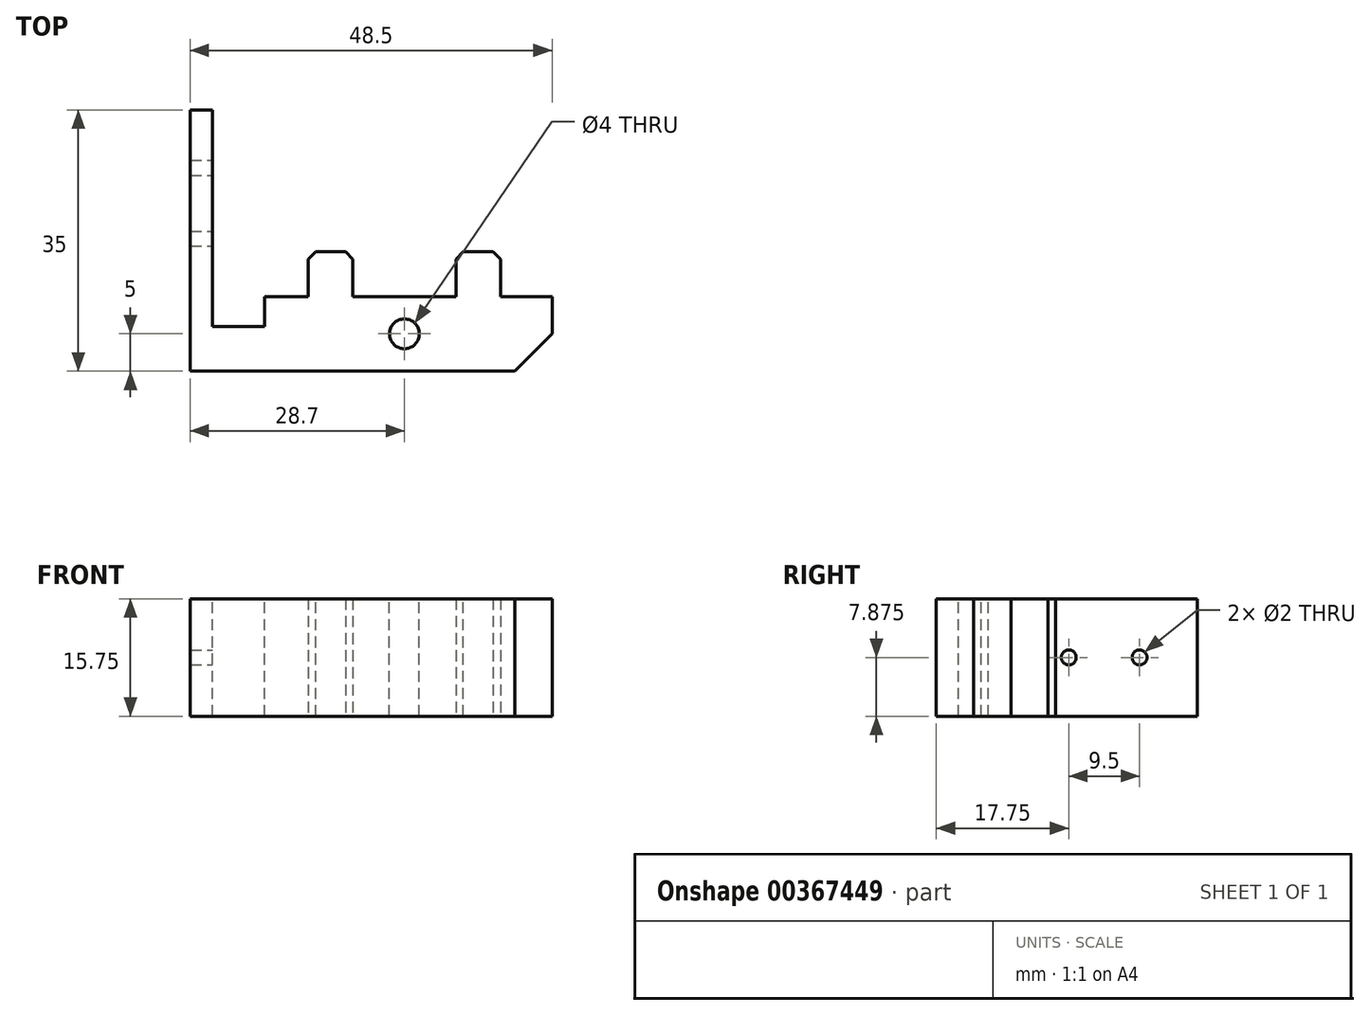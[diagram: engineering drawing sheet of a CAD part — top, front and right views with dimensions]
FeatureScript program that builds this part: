
annotation { "Feature Type Name" : "Feature", "Feature Type Description" : "" }
export const myFeature = defineFeature(function(context is Context, id is Id, definition is map)
    precondition{}
    {
        {
            var Q0;
            Q0=qCreatedBy(makeId("Top.planeOp"),FACE);
            var sketch = newSketch(context, id + "F0", { "sketchPlane" : qUnion([Q0])});
            skLineSegment(sketch, "E0", {"start": v(44.5, 0) * mm, "end": v(44.5, 10) * mm});
            skLineSegment(sketch, "E1", {"start": v(44.5, 10) * mm, "end": v(37.6, 10) * mm});
            skLineSegment(sketch, "E2", {"start": v(37.6, 10) * mm, "end": v(37.6, 16) * mm});
            skLineSegment(sketch, "E3", {"start": v(37.6, 16) * mm, "end": v(31.6, 16) * mm});
            skLineSegment(sketch, "E4", {"start": v(31.6, 16) * mm, "end": v(31.6, 10) * mm});
            skLineSegment(sketch, "E5", {"start": v(31.6, 10) * mm, "end": v(17.8, 10) * mm});
            skLineSegment(sketch, "E6", {"start": v(17.8, 10) * mm, "end": v(17.8, 16) * mm});
            skLineSegment(sketch, "E7", {"start": v(17.8, 16) * mm, "end": v(11.8, 16) * mm});
            skLineSegment(sketch, "E8", {"start": v(11.8, 16) * mm, "end": v(11.8, 10) * mm});
            skLineSegment(sketch, "E9", {"start": v(11.8, 10) * mm, "end": v(0, 10) * mm});
            skLineSegment(sketch, "E10", {"start": v(0, 0) * mm, "end": v(44.5, 0) * mm});
            skLineSegment(sketch, "E11", {"start": v(0, 10) * mm, "end": v(0, 0) * mm});
            skSolve(sketch);
        }
        {
            var Q0;
            Q0=qSketchRegion(id+"F0",true);
            extrude(context, id + "F1", {"entities" : qUnion([Q0]), "depth" : 15.75 * mm});
        }
        {
            var Q0;
            Q0=makeQuery(id+"F1.opExtrude","SWEPT_FACE",FACE,{"disambiguationData":[OSD([sQuery(id+"F0.wireOp",EDGE,"E10")])]});
            var sketch = newSketch(context, id + "F2", { "sketchPlane" : qUnion([Q0])});
            skLineSegment(sketch, "E12", {"start": v(0, 12.75) * mm, "end": v(15, 12.75) * mm});
            skLineSegment(sketch, "E13", {"start": v(15, 12.75) * mm, "end": v(15, 3) * mm});
            skLineSegment(sketch, "E14", {"start": v(15, 3) * mm, "end": v(0, 3) * mm});
            skLineSegment(sketch, "E15", {"start": v(0, 12.75) * mm, "end": v(0, 3) * mm});
            skSolve(sketch);
        }
        {
            var Q0;
            Q0=makeQuery(id+"F1.opExtrude","CAP_FACE",FACE,{"disambiguationData":[OSD([sQuery(id+"F0.wireOp",EDGE,"E0"),sQuery(id+"F0.wireOp",EDGE,"E1"),sQuery(id+"F0.wireOp",EDGE,"E2"),sQuery(id+"F0.wireOp",EDGE,"E3"),sQuery(id+"F0.wireOp",EDGE,"E4"),sQuery(id+"F0.wireOp",EDGE,"E5"),sQuery(id+"F0.wireOp",EDGE,"E6"),sQuery(id+"F0.wireOp",EDGE,"E7"),sQuery(id+"F0.wireOp",EDGE,"E8"),sQuery(id+"F0.wireOp",EDGE,"E9"),sQuery(id+"F0.wireOp",EDGE,"E10"),sQuery(id+"F0.wireOp",EDGE,"E11")])],"isStart":false});
            var sketch = newSketch(context, id + "F3", { "sketchPlane" : qUnion([Q0])});
            skPoint(sketch, "E16", {"position": v(24.7, 5) * mm});
            skPoint(sketch, "E16.positionSnap0", {"position": v(44.5, 5) * mm});
            skPoint(sketch, "E16.positionSnap1", {"position": v(24.7, 10) * mm});
            skSolve(sketch);
        }
        {
            var Q0;
            Q0=sQuery(id+"F3.wireOp",VERTEX,"E16");
            var Q1;
            Q1=makeQuery(id+"F1.opExtrude","SWEPT_BODY",BODY,{"disambiguationData":[OSD([sQuery(id+"F0.wireOp",EDGE,"E0"),sQuery(id+"F0.wireOp",EDGE,"E1"),sQuery(id+"F0.wireOp",EDGE,"E2"),sQuery(id+"F0.wireOp",EDGE,"E3"),sQuery(id+"F0.wireOp",EDGE,"E4"),sQuery(id+"F0.wireOp",EDGE,"E5"),sQuery(id+"F0.wireOp",EDGE,"E6"),sQuery(id+"F0.wireOp",EDGE,"E7"),sQuery(id+"F0.wireOp",EDGE,"E8"),sQuery(id+"F0.wireOp",EDGE,"E9"),sQuery(id+"F0.wireOp",EDGE,"E10"),sQuery(id+"F0.wireOp",EDGE,"E11")])]});
            hole(context, id + "F4", {"style" : HoleStyle.SIMPLE, "endStyle" : HoleEndStyle.THROUGH, "holeDiameter" : 4 * mm, "locations" : qUnion([Q0]), "scope" : qUnion([Q1]), "isTappedThrough" : true});
        }
        {
            var Q0;
            Q0=makeQuery(id+"F1.opExtrude","SWEPT_FACE",FACE,{"disambiguationData":[OSD([sQuery(id+"F0.wireOp",EDGE,"E11")])]});
            extrude(context, id + "F5", {"entities" : qUnion([Q0]), "operationType" : NewBodyOperationType.ADD, "depth" : 3 * mm});
        }
        {
            var Q0;
            {var subQ0=sQuery(id+"F0.wireOp",EDGE,"E9");Q0=makeQuery(id+"F5.boolean.opBoolean","MERGE",FACE,{"derivedFrom":[makeQuery(id+"F1.opExtrude","SWEPT_FACE",FACE,{"disambiguationData":[OSD([subQ0])]}),makeQuery(id+"F5.opExtrude","SWEPT_FACE",FACE,{"disambiguationData":[OSD([subQ0,sQuery(id+"F0.wireOp",EDGE,"E11")])]})]});}
            var sketch = newSketch(context, id + "F6", { "sketchPlane" : qUnion([Q0])});
            skLineSegment(sketch, "E17", {"start": v(0, 0) * mm, "end": v(0, 15.75) * mm});
            skSolve(sketch);
        }
        {
            var Q0;
            {var subQ0=sQuery(id+"F6.wireOp",EDGE,"E17");Q0=makeQuery(id+"F6.imprint","IMPRINT",FACE,{"disambiguationData":[TD([[makeQuery(id+"F6.imprint","IMPRINT",EDGE,{"derivedFrom":subQ0}),-1.0]])]});}
            extrude(context, id + "F7", {"entities" : qUnion([Q0]), "operationType" : NewBodyOperationType.ADD, "depth" : 25 * mm});
        }
        {
            var Q0;
            Q0=makeQuery(id+"F7.opExtrude","SWEPT_FACE",FACE,{"disambiguationData":[OSD([sQuery(id+"F6.wireOp",EDGE,"E17")])]});
            var sketch = newSketch(context, id + "F8", { "sketchPlane" : qUnion([Q0])});
            skPoint(sketch, "E18", {"position": v(27.25, 7.88) * mm});
            skPoint(sketch, "E18.positionSnap0", {"position": v(35, 7.88) * mm});
            skPoint(sketch, "E19", {"position": v(17.75, 7.88) * mm});
            skLineSegment(sketch, "E20", {"start": v(27.25, 7.88) * mm, "end": v(35, 7.88) * mm, "construction": true});
            skLineSegment(sketch, "E21", {"start": v(17.75, 7.88) * mm, "end": v(10, 7.88) * mm, "construction": true});
            skSolve(sketch);
        }
        {
            var Q0;
            Q0=sQuery(id+"F8.wireOp",VERTEX,"E18");
            var Q1;
            Q1=sQuery(id+"F8.wireOp",VERTEX,"E19");
            var Q2;
            Q2=makeQuery(id+"F1.opExtrude","SWEPT_BODY",BODY,{"disambiguationData":[OSD([sQuery(id+"F0.wireOp",EDGE,"E0"),sQuery(id+"F0.wireOp",EDGE,"E1"),sQuery(id+"F0.wireOp",EDGE,"E2"),sQuery(id+"F0.wireOp",EDGE,"E3"),sQuery(id+"F0.wireOp",EDGE,"E4"),sQuery(id+"F0.wireOp",EDGE,"E5"),sQuery(id+"F0.wireOp",EDGE,"E6"),sQuery(id+"F0.wireOp",EDGE,"E7"),sQuery(id+"F0.wireOp",EDGE,"E8"),sQuery(id+"F0.wireOp",EDGE,"E9"),sQuery(id+"F0.wireOp",EDGE,"E10"),sQuery(id+"F0.wireOp",EDGE,"E11")])]});
            hole(context, id + "F9", {"style" : HoleStyle.SIMPLE, "endStyle" : HoleEndStyle.THROUGH, "holeDiameter" : 2 * mm, "startFromSketch" : true, "locations" : qUnion([Q0, Q1]), "scope" : qUnion([Q2]), "isTappedThrough" : true});
        }
        {
            var Q0;
            {var subQ0=sQuery(id+"F0.wireOp",EDGE,"E11");var subQ1=sQuery(id+"F0.wireOp",EDGE,"E9");var subQ2=makeQuery(id+"F5.boolean.opBoolean","MERGE",EDGE,{"derivedFrom":[makeQuery(id+"F1.opExtrude","CAP_EDGE",EDGE,{"disambiguationData":[OSD([subQ1])],"isStart":false}),makeQuery(id+"F5.opExtrude","SWEPT_EDGE",EDGE,{"disambiguationData":[OSD([subQ1,subQ0]),TDD([makeQuery(id+"F1.opExtrude","CAP_VERTEX",VERTEX,{"disambiguationData":[OSD([subQ1,subQ0])],"isStart":false})])]})]});Q0=makeQuery(id+"F7.boolean.opBoolean","MERGE",FACE,{"derivedFrom":[makeQuery(id+"F5.boolean.opBoolean","MERGE",FACE,{"derivedFrom":[makeQuery(id+"F1.opExtrude","CAP_FACE",FACE,{"disambiguationData":[OSD([sQuery(id+"F0.wireOp",EDGE,"E0"),sQuery(id+"F0.wireOp",EDGE,"E1"),sQuery(id+"F0.wireOp",EDGE,"E2"),sQuery(id+"F0.wireOp",EDGE,"E3"),sQuery(id+"F0.wireOp",EDGE,"E4"),sQuery(id+"F0.wireOp",EDGE,"E5"),sQuery(id+"F0.wireOp",EDGE,"E6"),sQuery(id+"F0.wireOp",EDGE,"E7"),sQuery(id+"F0.wireOp",EDGE,"E8"),subQ1,sQuery(id+"F0.wireOp",EDGE,"E10"),subQ0])],"isStart":false}),makeQuery(id+"F5.opExtrude","SWEPT_FACE",FACE,{"disambiguationData":[OSD([subQ0]),TDD([makeQuery(id+"F1.opExtrude","CAP_EDGE",EDGE,{"disambiguationData":[OSD([subQ0])],"isStart":false})])]})]}),makeQuery(id+"F7.opExtrude","SWEPT_FACE",FACE,{"disambiguationData":[OSD([subQ1,subQ0]),TDD([makeQuery(id+"F6.imprint","IMPRINT",EDGE,{"disambiguationData":[TD([[makeQuery(id+"F6.imprint","INTERSECT",VERTEX,{"derivedFrom":[subQ2,sQuery(id+"F6.wireOp",EDGE,"E17")]}),-1.0]])],"derivedFrom":subQ2})])]})]});}
            var sketch = newSketch(context, id + "F10", { "sketchPlane" : qUnion([Q0])});
            skLineSegment(sketch, "E22", {"start": v(0, 10) * mm, "end": v(0, 6) * mm});
            skLineSegment(sketch, "E23", {"start": v(0, 6) * mm, "end": v(6, 6) * mm});
            skLineSegment(sketch, "E24", {"start": v(6, 6) * mm, "end": v(6, 10) * mm});
            skLineSegment(sketch, "E25", {"start": v(6, 10) * mm, "end": v(0, 10) * mm});
            skSolve(sketch);
        }
        {
            var Q0;
            Q0=qSketchRegion(id+"F10",true);
            extrude(context, id + "F11", {"entities" : qUnion([Q0]), "operationType" : NewBodyOperationType.REMOVE, "endBound" : BoundingType.THROUGH_ALL, "oppositeDirection" : true, "depth" : 25 * mm});
        }
        {
            var Q0;
            Q0=makeQuery(id+"F1.opExtrude","SWEPT_EDGE",EDGE,{"disambiguationData":[OSD([sQuery(id+"F0.wireOp",EDGE,"E7"),sQuery(id+"F0.wireOp",EDGE,"E8")])]});
            var Q1;
            Q1=makeQuery(id+"F1.opExtrude","SWEPT_EDGE",EDGE,{"disambiguationData":[OSD([sQuery(id+"F0.wireOp",EDGE,"E6"),sQuery(id+"F0.wireOp",EDGE,"E7")])]});
            var Q2;
            Q2=makeQuery(id+"F1.opExtrude","SWEPT_EDGE",EDGE,{"disambiguationData":[OSD([sQuery(id+"F0.wireOp",EDGE,"E3"),sQuery(id+"F0.wireOp",EDGE,"E4")])]});
            var Q3;
            Q3=makeQuery(id+"F1.opExtrude","SWEPT_EDGE",EDGE,{"disambiguationData":[OSD([sQuery(id+"F0.wireOp",EDGE,"E2"),sQuery(id+"F0.wireOp",EDGE,"E3")])]});
            chamfer(context, id + "F12", {"entities" : qUnion([Q0, Q1, Q2, Q3]), "width" : 1 * mm, "tangentPropagation" : true});
        }
        {
            var Q0;
            Q0=makeQuery(id+"F1.opExtrude","SWEPT_EDGE",EDGE,{"disambiguationData":[OSD([sQuery(id+"F0.wireOp",EDGE,"E0"),sQuery(id+"F0.wireOp",EDGE,"E10")])]});
            chamfer(context, id + "F13", {"entities" : qUnion([Q0]), "width" : 5 * mm, "tangentPropagation" : true});
        }
        {
            var Q0;
            {var subQ0=sQuery(id+"F0.wireOp",EDGE,"E11");var subQ1=sQuery(id+"F0.wireOp",EDGE,"E9");Q0=makeQuery(id+"F7.boolean.opBoolean","MERGE",FACE,{"derivedFrom":[makeQuery(id+"F5.opExtrude","CAP_FACE",FACE,{"disambiguationData":[OSD([subQ0])],"isStart":false}),makeQuery(id+"F7.opExtrude","SWEPT_FACE",FACE,{"disambiguationData":[OSD([subQ1,subQ0]),TDD([makeQuery(id+"F6.imprint","IMPRINT",EDGE,{"derivedFrom":makeQuery(id+"F5.opExtrude","CAP_EDGE",EDGE,{"disambiguationData":[OSD([subQ1,subQ0])],"isStart":false})})])]})]});}
            extrude(context, id + "F14", {"entities" : qUnion([Q0]), "operationType" : NewBodyOperationType.ADD, "depth" : 1 * mm});
        }
        {
            var Q0;
            Q0=makeQuery(id+"F11.boolean.opBoolean","MERGE",FACE,{"derivedFrom":[makeQuery(id+"F7.opExtrude","SWEPT_FACE",FACE,{"disambiguationData":[OSD([sQuery(id+"F6.wireOp",EDGE,"E17")])]}),makeQuery(id+"F11.opExtrude","SWEPT_FACE",FACE,{"disambiguationData":[OSD([sQuery(id+"F10.wireOp",EDGE,"E22")])]})]});
            extrude(context, id + "F15", {"entities" : qUnion([Q0]), "operationType" : NewBodyOperationType.REMOVE, "oppositeDirection" : true, "depth" : 1 * mm});
        }
    });
